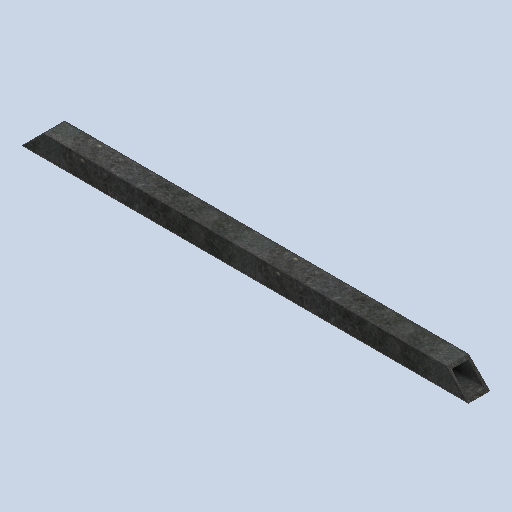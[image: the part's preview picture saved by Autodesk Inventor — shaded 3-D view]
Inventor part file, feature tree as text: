
AUTODESK INVENTOR PART (.ipt)
format: ipt  version: 2024.3 (Build 283343000, 343)  size: 253,440 bytes
history: native  units: mm
features: extrude x2, sketch x2
ambient origin geometry x8: Origin, YZ Plane, XZ Plane, XY Plane, X Axis, Y Axis, Z Axis, Center Point
bodies: Solid1 (feature_tree)
feature tree (4):
  extrude  "Extrusion1"  Depth=2.0mm
  extrude  "Extrusion2"  Depth=19.0mm
  sketch  "Sketch1"  dims[d0=2.0mm d1=2.0mm]
  sketch  "Sketch2"  dims[d2=19.0mm d3=19.0mm d4=400.0mm d5=0.0mm d8=10.0mm d9=0.0mm d10=45.0deg d11=45.0deg]
